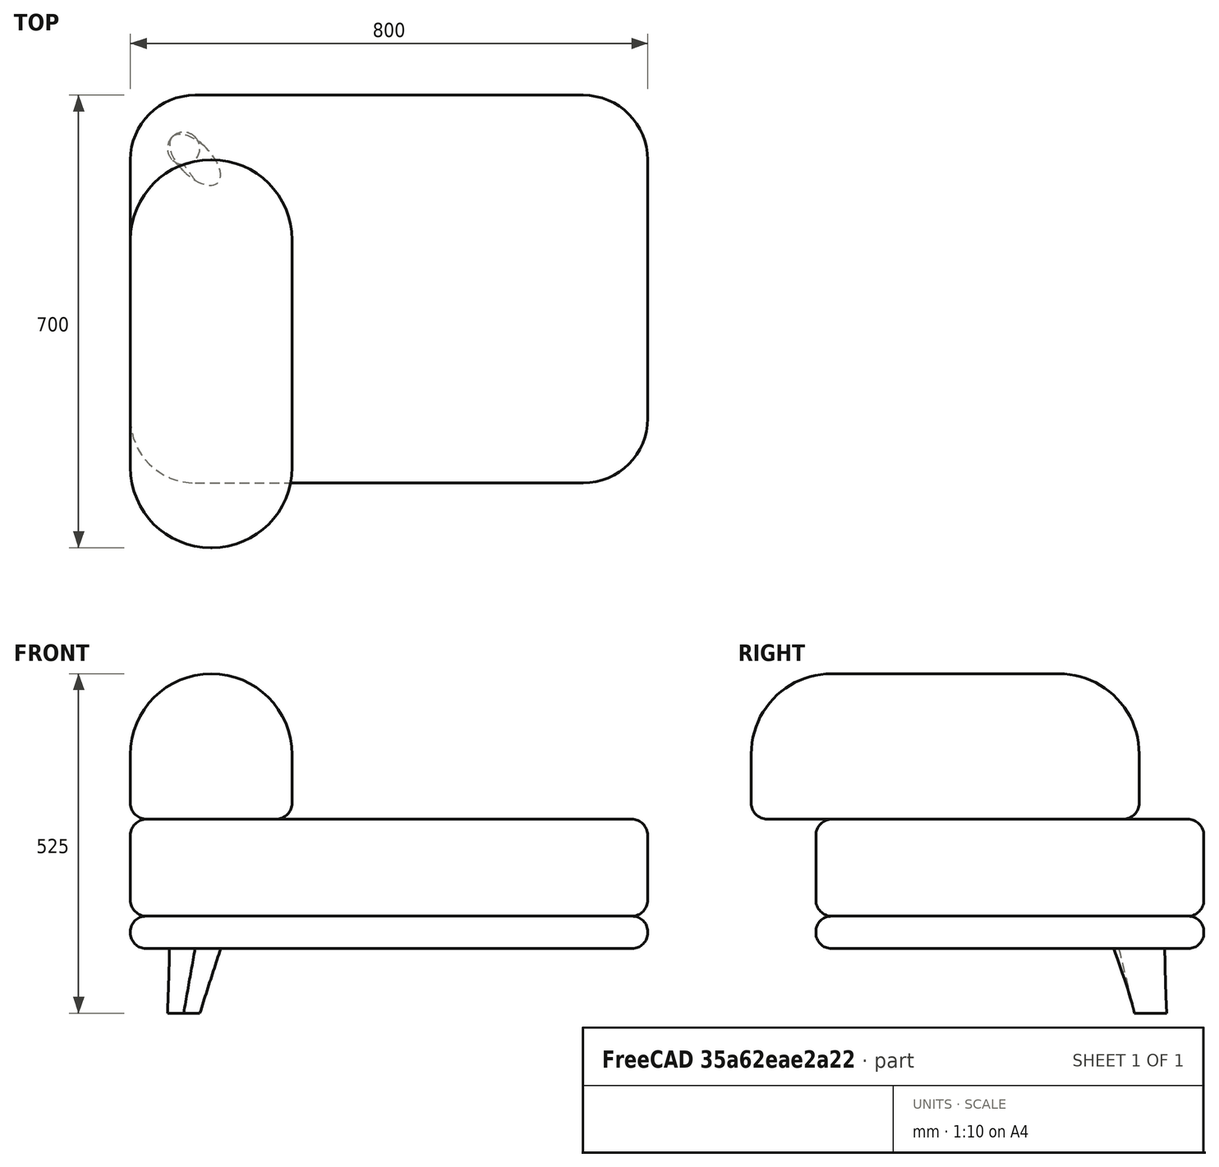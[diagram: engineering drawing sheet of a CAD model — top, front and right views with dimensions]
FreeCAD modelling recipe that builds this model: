
FCSTD DOCUMENT  (FreeCAD 1.0R39319 (Git))
Label: Drawing room Sofa center
License: All rights reserved
objects: App::Link×7, App::FeaturePython×7, Sketcher::SketchObject×5, PartDesign::Fillet×4, PartDesign::Body×4, PartDesign::Pad×3, PartDesign::Plane×1, PartDesign::AdditiveLoft×1, Assembly::JointGroup×1, Assembly::AssemblyObject×1
note: 39 computed .brp shape members not serialized (recipe doc carries the construction recipe); baked Part::Feature solids carry a one-line shape summary decoded from their .brp

FEATURE [Sketcher::SketchObject] Sketch
  ArcFitTolerance = 1e-06
  AttachmentSupport = -> [XY_Plane]
  FullyConstrained = true
  MakeInternals = false
  MapMode = 5
  sketch-geometry (18):
    g0: LineSegment StartX=0 StartY=-100 StartZ=0 EndX=0 EndY=-500 EndZ=0
    g1: LineSegment StartX=100 StartY=-600 StartZ=0 EndX=700 EndY=-600 EndZ=0
    g2: LineSegment StartX=800 StartY=-500 StartZ=0 EndX=800 EndY=-100 EndZ=0
    g3: LineSegment StartX=700 StartY=0 StartZ=0 EndX=100 EndY=0 EndZ=0
    g4: ArcOfCircle CenterX=100 CenterY=-100 CenterZ=0 NormalX=0 NormalY=0 NormalZ=1 AngleXU=0 Radius=100 StartAngle=1.5708 EndAngle=3.14159
    g5: ArcOfCircle CenterX=100 CenterY=-500 CenterZ=0 NormalX=0 NormalY=0 NormalZ=1 AngleXU=0 Radius=100 StartAngle=3.14159 EndAngle=4.71239
    g6: ArcOfCircle CenterX=700 CenterY=-500 CenterZ=0 NormalX=0 NormalY=0 NormalZ=1 AngleXU=0 Radius=100 StartAngle=4.71239 EndAngle=6.28319
    g7: ArcOfCircle CenterX=700 CenterY=-100 CenterZ=0 NormalX=0 NormalY=0 NormalZ=1 AngleXU=0 Radius=100 StartAngle=0 EndAngle=1.5708
    g8: LineSegment [constr] StartX=25 StartY=-100 StartZ=0 EndX=25 EndY=-500 EndZ=0
    g9: LineSegment [constr] StartX=100 StartY=-575 StartZ=0 EndX=700 EndY=-575 EndZ=0
    g10: LineSegment [constr] StartX=775 StartY=-500 StartZ=0 EndX=775 EndY=-100 EndZ=0
    g11: LineSegment [constr] StartX=700 StartY=-25 StartZ=0 EndX=100 EndY=-25 EndZ=0
    g12: ArcOfCircle [constr] CenterX=100 CenterY=-100 CenterZ=0 NormalX=0 NormalY=0 NormalZ=1 AngleXU=0 Radius=75 StartAngle=1.5708 EndAngle=3.14159
    g13: ArcOfCircle [constr] CenterX=100 CenterY=-500 CenterZ=0 NormalX=0 NormalY=0 NormalZ=1 AngleXU=0 Radius=75 StartAngle=3.14159 EndAngle=4.71239
    g14: ArcOfCircle [constr] CenterX=700 CenterY=-500 CenterZ=0 NormalX=0 NormalY=0 NormalZ=1 AngleXU=0 Radius=75 StartAngle=4.71239 EndAngle=6.28319
    g15: ArcOfCircle [constr] CenterX=700 CenterY=-100 CenterZ=0 NormalX=0 NormalY=0 NormalZ=1 AngleXU=0 Radius=75 StartAngle=0 EndAngle=1.5708
    g16: GeomPoint [constr] X=0 Y=0 Z=0
    g17: GeomPoint [constr] X=800 Y=-600 Z=0
  constraints (39):
    c: Tangent(g0,g4) = -1.5708
    c: Tangent(g0,g5) = -1.5708
    c: Tangent(g1,g5) = -1.5708
    c: Tangent(g1,g6) = -1.5708
    c: Tangent(g2,g6) = -1.5708
    c: Tangent(g2,g7) = -1.5708
    c: Tangent(g3,g7) = -1.5708
    c: Tangent(g3,g4) = -1.5708
    c: Vertical(g0)
    c: Vertical(g2)
    c: Horizontal(g1)
    c: Horizontal(g3)
    c: Equal(g4,g5)
    c: Equal(g5,g6)
    c: Equal(g6,g7)
    c: Tangent(g8,g12) = -1.5708
    c: Tangent(g8,g13) = -1.5708
    c: Tangent(g9,g13) = -1.5708
    c: Tangent(g9,g14) = -1.5708
    c: Tangent(g10,g14) = -1.5708
    c: Tangent(g10,g15) = -1.5708
    c: Tangent(g11,g15) = -1.5708
    c: Tangent(g11,g12) = -1.5708
    c: Coincident(g4,g12)
    c: Coincident(g5,g13)
    c: Coincident(g6,g14)
    c: Coincident(g7,g15)
    c: Vertical(g8)
    c: Vertical(g10)
    c: Horizontal(g9)
    c: PointOnObject(g16,g0)
    c: PointOnObject(g16,g3)
    c: PointOnObject(g17,g1)
    c: PointOnObject(g17,g2)
    c: Distance(g0,g2) = 800
    c: Distance(g1,g3) = 600
    c: Radius(g5) = 100
    c: Distance(g8,g0) = 25
    c: Coincident(g16,g-1)
FEATURE [PartDesign::Pad] Pad
  Direction = (0,0,1)
  Length = 50
  Length2 = 10
  Profile = -> Sketch
  ReferenceAxis = -> Sketch [N_Axis]
  Refine = true
  Suppressed = false
  Type = 0
FEATURE [Sketcher::SketchObject] Sketch001
  ArcFitTolerance = 1e-06
  AttachmentSupport = -> [XY_Plane001]
  FullyConstrained = true
  MakeInternals = false
  MapMode = 5
  sketch-geometry (10):
    g0: LineSegment StartX=6.963e-13 StartY=-100 StartZ=0 EndX=6.963e-13 EndY=-500 EndZ=0
    g1: LineSegment StartX=100 StartY=-600 StartZ=0 EndX=700 EndY=-600 EndZ=0
    g2: LineSegment StartX=800 StartY=-500 StartZ=0 EndX=800 EndY=-100 EndZ=0
    g3: LineSegment StartX=700 StartY=-8.242e-13 StartZ=0 EndX=100 EndY=-8.242e-13 EndZ=0
    g4: ArcOfCircle CenterX=100 CenterY=-100 CenterZ=0 NormalX=0 NormalY=0 NormalZ=1 AngleXU=0 Radius=100 StartAngle=1.5708 EndAngle=3.14159
    g5: ArcOfCircle CenterX=100 CenterY=-500 CenterZ=0 NormalX=0 NormalY=0 NormalZ=1 AngleXU=0 Radius=100 StartAngle=3.14159 EndAngle=4.71239
    g6: ArcOfCircle CenterX=700 CenterY=-500 CenterZ=0 NormalX=0 NormalY=0 NormalZ=1 AngleXU=0 Radius=100 StartAngle=4.71239 EndAngle=6.28319
    g7: ArcOfCircle CenterX=700 CenterY=-100 CenterZ=0 NormalX=0 NormalY=0 NormalZ=1 AngleXU=0 Radius=100 StartAngle=7e-14 EndAngle=1.5708
    g8: GeomPoint [constr] X=0 Y=0 Z=0
    g9: GeomPoint [constr] X=800 Y=-600 Z=0
  constraints (23):
    c: Tangent(g0,g4) = -1.5708
    c: Tangent(g0,g5) = -1.5708
    c: Tangent(g1,g5) = -1.5708
    c: Tangent(g1,g6) = -1.5708
    c: Tangent(g2,g6) = -1.5708
    c: Tangent(g2,g7) = -1.5708
    c: Tangent(g3,g7) = -1.5708
    c: Tangent(g3,g4) = -1.5708
    c: Vertical(g0)
    c: Vertical(g2)
    c: Horizontal(g1)
    c: Horizontal(g3)
    c: Equal(g4,g5)
    c: Equal(g5,g6)
    c: Equal(g6,g7)
    c: PointOnObject(g8,g0)
    c: PointOnObject(g8,g3)
    c: PointOnObject(g9,g1)
    c: PointOnObject(g9,g2)
    c: Distance(g0,g2) = 800
    c: Distance(g1,g3) = 600
    c: Radius(g5) = 100
    c: Coincident(g8,g-1)
FEATURE [PartDesign::Pad] Pad001
  Direction = (0,0,1)
  Length = 150
  Length2 = 10
  Profile = -> Sketch001
  ReferenceAxis = -> Sketch001 [N_Axis]
  Refine = true
  Suppressed = false
  Type = 0
FEATURE [PartDesign::Fillet] Fillet
  Base = -> Pad001 [Edge16,Edge19,Edge22,Edge24,Edge4,Edge7,Edge10,Edge13,Edge21,Edge23,Edge3,Edge6,Edge9,Edge12,Edge15,Edge18]
  BaseFeature = -> Pad001
  Radius = 25
  Refine = true
  SupportTransform = false
  Suppressed = false
  UseAllEdges = false
FEATURE [PartDesign::Body] Body001  label="Cushion"
  AllowCompound = false
  Group = -> [Sketch001,Pad001,Fillet]
  Origin = -> Origin001
  Placement = pos=(0,0,50) rot=(0,0,1;0rad)
  Tip = -> Fillet
FEATURE [PartDesign::Fillet] Fillet001
  Base = -> Pad [Face10]
  BaseFeature = -> Pad
  Radius = 24
  Refine = true
  SupportTransform = false
  Suppressed = false
  UseAllEdges = true
FEATURE [PartDesign::Body] Body  label="Base"
  AllowCompound = false
  Group = -> [Sketch,Pad,Fillet001]
  Origin = -> Origin
  Tip = -> Fillet001
FEATURE [Sketcher::SketchObject] Sketch002
  ArcFitTolerance = 1e-06
  AttachmentSupport = -> [XZ_Plane002]
  FullyConstrained = true
  MakeInternals = false
  MapMode = 5
  Placement = pos=(0,0,0) rot=(1,0,0;1.5708rad)
  sketch-geometry (5):
    g0: LineSegment StartX=0 StartY=0 StartZ=0 EndX=250 EndY=0 EndZ=0
    g1: LineSegment StartX=250 StartY=0 StartZ=0 EndX=250 EndY=100 EndZ=0
    g2: LineSegment [constr] StartX=250 StartY=100 StartZ=0 EndX=0 EndY=100 EndZ=0
    g3: LineSegment StartX=0 StartY=100 StartZ=0 EndX=0 EndY=0 EndZ=0
    g4: ArcOfCircle CenterX=125 CenterY=100 CenterZ=0 NormalX=0 NormalY=0 NormalZ=1 AngleXU=0 Radius=125 StartAngle=0 EndAngle=3.14159
  constraints (14):
    c: Coincident(g0,g1)
    c: Coincident(g1,g2)
    c: Coincident(g2,g3)
    c: Coincident(g3,g0)
    c: Horizontal(g0)
    c: Horizontal(g2)
    c: Vertical(g1)
    c: Vertical(g3)
    c: Distance(g1,g3) = 250
    c: Distance(g0,g2) = 100
    c: Coincident(g0,g-1)
    c: Coincident(g4,g2)
    c: Coincident(g4,g1)
    c: PointOnObject(g4,g2)
FEATURE [PartDesign::Pad] Pad002
  Direction = (0,-1,2e-16)
  Length = 600
  Length2 = 10
  Placement = pos=(0,0,0) rot=(1,0,0;1.5708rad)
  Profile = -> Sketch002
  ReferenceAxis = -> Sketch002 [N_Axis]
  Refine = true
  Suppressed = false
  Type = 0
FEATURE [PartDesign::Fillet] Fillet002
  Base = -> Pad002 [Edge9,Edge10]
  BaseFeature = -> Pad002
  Placement = pos=(0,0,0) rot=(1,0,0;1.5708rad)
  Radius = 124
  Refine = true
  SupportTransform = false
  Suppressed = false
  UseAllEdges = false
FEATURE [PartDesign::Fillet] Fillet003
  Base = -> Fillet002 [Face1]
  BaseFeature = -> Fillet002
  Placement = pos=(0,0,0) rot=(1,0,0;1.5708rad)
  Radius = 25
  Refine = true
  SupportTransform = false
  Suppressed = false
  UseAllEdges = true
FEATURE [PartDesign::Body] Body002  label="Backrest"
  AllowCompound = false
  Group = -> [Sketch002,Pad002,Fillet002,Fillet003]
  Origin = -> Origin002
  Placement = pos=(0,-100,200) rot=(0,0,1;0rad)
  Tip = -> Fillet003
FEATURE [Sketcher::SketchObject] Sketch003
  ArcFitTolerance = 1e-06
  AttachmentSupport = -> [XY_Plane003]
  FullyConstrained = true
  MakeInternals = false
  MapMode = 5
  sketch-geometry (5):
    g0: Ellipse CenterX=0 CenterY=0 CenterZ=0 NormalX=0 NormalY=0 NormalZ=1 MajorRadius=50 MinorRadius=25 AngleXU=-2.35619
    g1: LineSegment [constr] StartX=-35.3553 StartY=-35.3553 StartZ=0 EndX=35.3553 EndY=35.3553 EndZ=0
    g2: LineSegment [constr] StartX=17.6777 StartY=-17.6777 StartZ=0 EndX=-17.6777 EndY=17.6777 EndZ=0
    g3: GeomPoint [constr] X=-30.6186 Y=-30.6186 Z=0
    g4: GeomPoint [constr] X=30.6186 Y=30.6186 Z=0
  constraints (5):
    c: InternalAlignment(g1-g4 -> g0) x4
    c: Distance(g0,g1) = 50
    c: Angle(g1) = 0.785398
    c: Distance(g0,g2) = 25
    c: Coincident(g0,g-1)
FEATURE [PartDesign::Plane] DatumPlane
  AttachmentOffset = pos=(0,0,-100) rot=(0,0,1;0rad)
  AttachmentSupport = -> [Sketch003]
  Length = 60
  MapMode = 2
  Placement = pos=(0,0,-100) rot=(0,0,1;0rad)
  ResizeMode = 0
  Width = 60
FEATURE [Sketcher::SketchObject] Sketch004
  ArcFitTolerance = 1e-06
  AttachmentSupport = -> [DatumPlane]
  FullyConstrained = true
  MakeInternals = false
  MapMode = 5
  Placement = pos=(0,0,-100) rot=(0,0,1;0rad)
  sketch-geometry (2):
    g0: Circle CenterX=-17.6777 CenterY=-17.6777 CenterZ=0 NormalX=0 NormalY=0 NormalZ=1 AngleXU=0 Radius=25
    g1: LineSegment [constr] StartX=-17.6777 StartY=-17.6777 StartZ=0 EndX=2.4e-15 EndY=4.5e-15 EndZ=0
  constraints (5):
    c: Diameter(g0) = 50
    c: Coincident(g1,g0)
    c: Coincident(g1,g-1)
    c: Angle(g1,g-1) = 2.35619
    c: PointOnObject(g1,g0)
FEATURE [PartDesign::AdditiveLoft] AdditiveLoft
  Closed = false
  Profile = -> Sketch003
  Refine = true
  Ruled = false
  Sections = -> [Sketch004]
  Suppressed = false
FEATURE [PartDesign::Body] Body003  label="Legs"
  AllowCompound = false
  Group = -> [Sketch003,DatumPlane,Sketch004,AdditiveLoft]
  Origin = -> Origin003
  Placement = pos=(100,-100,0) rot=(0,0,1;-1.5708rad)
  Tip = -> AdditiveLoft
FEATURE [App::Link] Base  label="Base001"
  LinkedObject = -> Body
FEATURE [App::FeaturePython] GroundedJoint  # Assembly grounded joint (typed FeaturePython)
  ObjectToGround = -> Base
FEATURE [App::Link] Cushion  label="Cushion001"
  LinkPlacement = pos=(-3.25e-14,2.84e-14,50) rot=(0,0,1;0rad)
  LinkedObject = -> Body001
  Placement = pos=(-3.25e-14,2.84e-14,50) rot=(0,0,1;0rad)
FEATURE [App::Link] Backrest  label="Backrest001"
  LinkPlacement = pos=(-1.91e-14,0,200) rot=(0,0,1;0rad)
  LinkedObject = -> Body002
  Placement = pos=(-1.91e-14,0,200) rot=(0,0,1;0rad)
FEATURE [App::Link] Legs  label="Legs001"
  LinkPlacement = pos=(700,0,0) rot=(0,0,1;3.14159rad)
  LinkedObject = -> Body003
  Placement = pos=(700,0,0) rot=(0,0,1;3.14159rad)
FEATURE [App::Link] Legs001  label="Legs002"
  LinkPlacement = pos=(100,-600,0) rot=(0,0,1;0rad)
  LinkedObject = -> Body003
  Placement = pos=(100,-600,0) rot=(0,0,1;0rad)
FEATURE [App::Link] Legs002  label="Legs003"
  LinkPlacement = pos=(700,-600,0) rot=(0,0,1;1.5708rad)
  LinkedObject = -> Body003
  Placement = pos=(700,-600,0) rot=(0,0,1;1.5708rad)
FEATURE [App::Link] Legs003  label="Legs004"
  LinkPlacement = pos=(100,-6e-15,0) rot=(0,0,-1;1.5708rad)
  LinkedObject = -> Body003
  Placement = pos=(100,-6e-15,0) rot=(0,0,-1;1.5708rad)
FEATURE [App::FeaturePython] Joint  label="Fixed"  # Assembly joint (typed FeaturePython)
  Activated = true
  AngleMax = 0
  AngleMin = 0
  Detach1 = false
  Detach2 = false
  Distance = 0
  Distance2 = 0
  EnableAngleMax = false
  EnableAngleMin = false
  EnableLengthMax = false
  EnableLengthMin = false
  JointType = 0 (Fixed)
  LengthMax = 0
  LengthMin = 0
  Placement1 = pos=(400,-300,50) rot=(0,0,1;0rad)
  Placement2 = pos=(400,-300,0) rot=(0,0,1;0rad)
  Reference1 = -> Assembly [Base.Face11,Base.Face11]
  Reference2 = -> Assembly [Cushion.Face9,Cushion.Face9]
FEATURE [App::FeaturePython] Joint001  label="Fixed001"  # Assembly joint (typed FeaturePython)
  Activated = true
  AngleMax = 0
  AngleMin = 0
  Detach1 = false
  Detach2 = false
  Distance = 0
  Distance2 = 0
  EnableAngleMax = false
  EnableAngleMin = false
  EnableLengthMax = false
  EnableLengthMin = false
  JointType = 0 (Fixed)
  LengthMax = 0
  LengthMin = 0
  Offset1 = pos=(275,0,0) rot=(0,0,1;0rad)
  Placement1 = pos=(400,-300,5.68e-14) rot=(0,0,1;0rad)
  Placement2 = pos=(400,-300,150) rot=(0,0,1;0rad)
  Reference1 = -> Assembly [Backrest.Face1,Backrest.Face1]
  Reference2 = -> Assembly [Cushion.Face11,Cushion.Face11]
FEATURE [App::FeaturePython] Joint002  label="Fixed002"  # Assembly joint (typed FeaturePython)
  Activated = true
  AngleMax = 0
  AngleMin = 0
  Detach1 = false
  Detach2 = false
  Distance = 0
  Distance2 = 0
  EnableAngleMax = false
  EnableAngleMin = false
  EnableLengthMax = false
  EnableLengthMin = false
  JointType = 0 (Fixed)
  LengthMax = 0
  LengthMin = 0
  Offset1 = pos=(300,300,0) rot=(0,0,1;0rad)
  Offset2 = pos=(0,0,0) rot=(0,0,1;3.14159rad)
  Placement1 = pos=(700,0,0) rot=(0,0,1;0rad)
  Placement2 = pos=(0,0,0) rot=(0,0,1;3.14159rad)
  Reference1 = -> Assembly [Base.Face9,Base.Face9]
  Reference2 = -> Assembly [Legs.Face1,Legs.Face1]
FEATURE [App::FeaturePython] Joint003  label="Fixed003"  # Assembly joint (typed FeaturePython)
  Activated = true
  AngleMax = 0
  AngleMin = 0
  Detach1 = false
  Detach2 = false
  Distance = 0
  Distance2 = 0
  EnableAngleMax = false
  EnableAngleMin = false
  EnableLengthMax = false
  EnableLengthMin = false
  JointType = 0 (Fixed)
  LengthMax = 0
  LengthMin = 0
  Offset1 = pos=(-300,-300,0) rot=(0,0,1;0rad)
  Placement1 = pos=(100,-600,0) rot=(0,0,1;0rad)
  Reference1 = -> Assembly [Base.Face9,Base.Face9]
  Reference2 = -> Assembly [Legs001.Face1,Legs001.Face1]
FEATURE [App::FeaturePython] Joint004  label="Fixed004"  # Assembly joint (typed FeaturePython)
  Activated = true
  AngleMax = 0
  AngleMin = 0
  Detach1 = false
  Detach2 = false
  Distance = 0
  Distance2 = 0
  EnableAngleMax = false
  EnableAngleMin = false
  EnableLengthMax = false
  EnableLengthMin = false
  JointType = 0 (Fixed)
  LengthMax = 0
  LengthMin = 0
  Offset1 = pos=(300,-300,0) rot=(0,0,1;1.5708rad)
  Placement1 = pos=(700,-600,0) rot=(0,0,1;1.5708rad)
  Reference1 = -> Assembly [Base.Face9,Base.Face9]
  Reference2 = -> Assembly [Legs002.Face1,Legs002.Face1]
FEATURE [App::FeaturePython] Joint005  label="Fixed005"  # Assembly joint (typed FeaturePython)
  Activated = true
  AngleMax = 0
  AngleMin = 0
  Detach1 = false
  Detach2 = false
  Distance = 0
  Distance2 = 0
  EnableAngleMax = false
  EnableAngleMin = false
  EnableLengthMax = false
  EnableLengthMin = false
  JointType = 0 (Fixed)
  LengthMax = 0
  LengthMin = 0
  Offset1 = pos=(-300,300,0) rot=(0,0,-1;1.5708rad)
  Placement1 = pos=(100,0,0) rot=(0,0,-1;1.5708rad)
  Placement2 = pos=(-6e-15,0,0) rot=(0,0,1;0rad)
  Reference1 = -> Assembly [Base.Face9,Base.Face9]
  Reference2 = -> Assembly [Legs003.Face1,Legs003.Face1]
FEATURE [Assembly::JointGroup] Joints
  Group = -> [GroundedJoint,Joint,Joint001,Joint002,Joint003,Joint004,Joint005]
FEATURE [Assembly::AssemblyObject] Assembly
  Group = -> [Joints,Base,GroundedJoint,Cushion,Backrest,Legs,Legs001,Legs002,Legs003,Joint,Joint001,Joint002,Joint003,Joint004,Joint005]
  Origin = -> Origin004
  Type = Assembly
